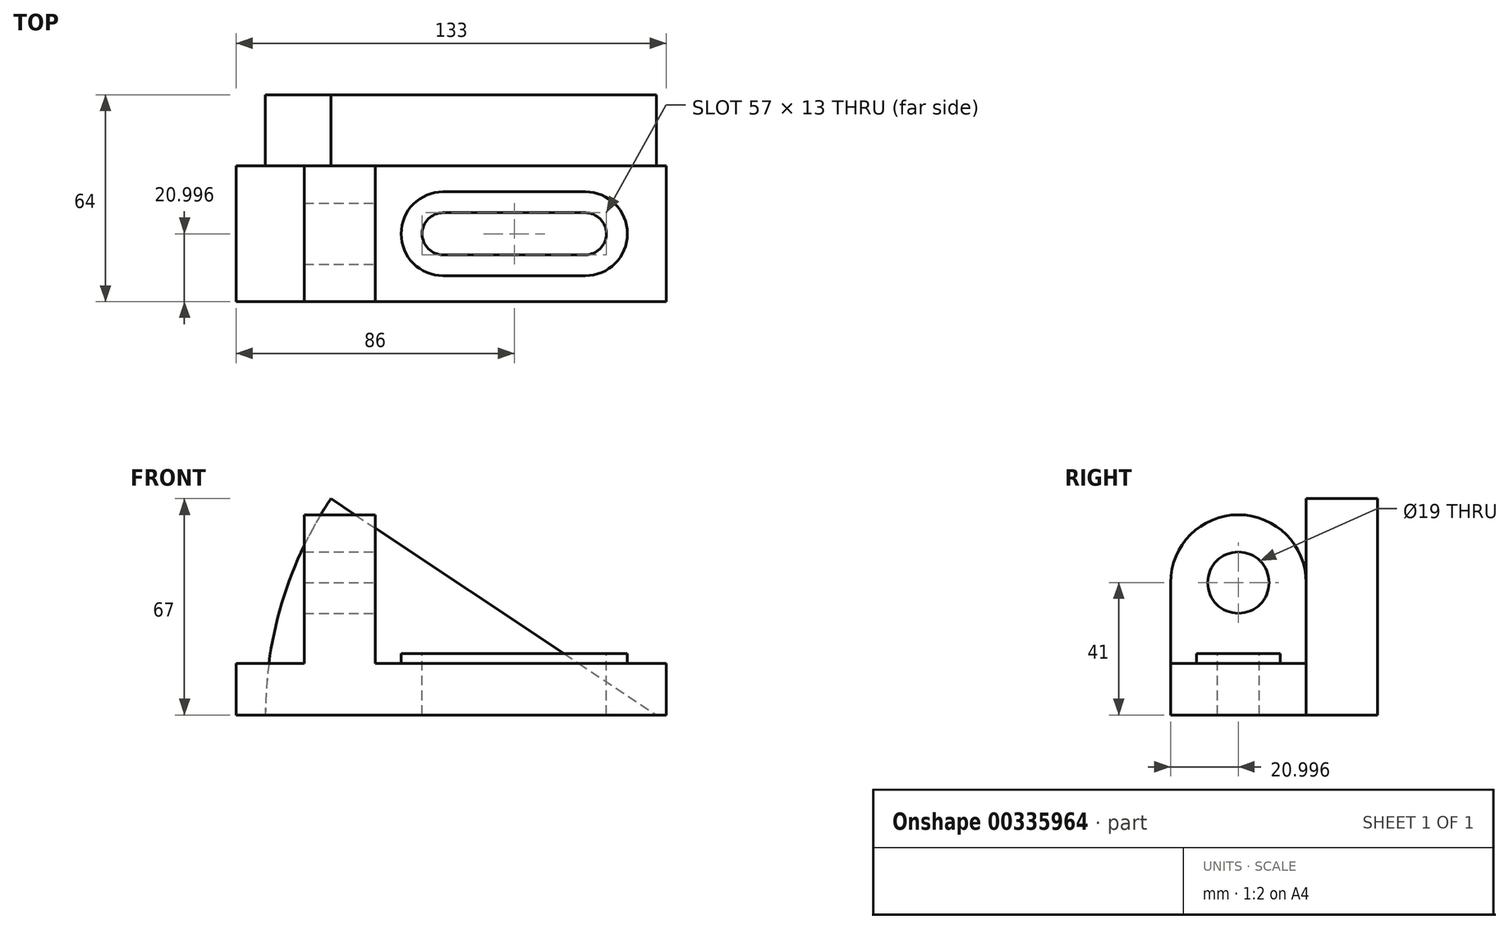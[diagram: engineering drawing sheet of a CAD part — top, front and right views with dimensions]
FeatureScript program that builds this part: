
annotation { "Feature Type Name" : "Feature", "Feature Type Description" : "" }
export const myFeature = defineFeature(function(context is Context, id is Id, definition is map)
    precondition{}
    {
        {
            var Q0;
            Q0=qCreatedBy(makeId("Right.planeOp"),FACE);
            var sketch = newSketch(context, id + "F0", { "sketchPlane" : qUnion([Q0])});
            skLineSegment(sketch, "E0.bottom", {"start": v(3.05, 24.2) * mm, "end": v(45.05, 24.2) * mm});
            skLineSegment(sketch, "E0.top", {"start": v(3.05, 8.2) * mm, "end": v(45.05, 8.2) * mm});
            skLineSegment(sketch, "E0.left", {"start": v(3.05, 24.2) * mm, "end": v(3.05, 8.2) * mm});
            skLineSegment(sketch, "E0.right", {"start": v(45.05, 24.2) * mm, "end": v(45.05, 8.2) * mm});
            skSolve(sketch);
        }
        {
            var Q0;
            Q0 = qSketchRegion(id + "F0", true);
            extrude(context, id + "F1", {"entities" : qUnion([Q0]), "oppositeDirection" : true, "depth" : 90 * mm});
        }
        {
            var Q0;
            Q0=makeQuery(id+"F1.opExtrude","CAP_FACE",FACE,{"disambiguationData":[OSD([sQuery(id+"F0.wireOp",EDGE,"E0.bottom"),sQuery(id+"F0.wireOp",EDGE,"E0.top"),sQuery(id+"F0.wireOp",EDGE,"E0.left"),sQuery(id+"F0.wireOp",EDGE,"E0.right")])],"isStart":false});
            var sketch = newSketch(context, id + "F2", { "sketchPlane" : qUnion([Q0])});
            skLineSegment(sketch, "E1", {"start": v(-45.05, 24.2) * mm, "end": v(-45.05, 49.2) * mm});
            skLineSegment(sketch, "E2", {"start": v(-45.05, 49.2) * mm, "end": v(-3.05, 49.2) * mm});
            skLineSegment(sketch, "E3", {"start": v(-3.05, 49.2) * mm, "end": v(-3.05, 24.2) * mm});
            skLineSegment(sketch, "E4", {"start": v(-3.05, 24.2) * mm, "end": v(-3.05, 8.2) * mm});
            skLineSegment(sketch, "E5", {"start": v(-3.05, 8.2) * mm, "end": v(-45.05, 8.2) * mm});
            skLineSegment(sketch, "E6", {"start": v(-45.05, 8.2) * mm, "end": v(-45.05, 24.2) * mm});
            skArc(sketch, "E7", {"start": v(-3.05, 49.2) * mm, "mid": v(-24.05, 70.2) * mm, "end": v(-45.05, 49.2) * mm});
            skCircle(sketch, "E8", {"center": v(-24.05, 49.2) * mm, "radius": 9.5 * mm});
            skSolve(sketch);
        }
        {
            var Q0;
            Q0 = qSketchRegion(id + "F2", true);
            extrude(context, id + "F3", {"entities" : qUnion([Q0]), "operationType" : NewBodyOperationType.ADD, "depth" : 22 * mm});
        }
        {
            var Q0;
            Q0=makeQuery(id+"F3.opExtrude","CAP_FACE",FACE,{"disambiguationData":[OSD([sQuery(id+"F2.wireOp",EDGE,"E1"),sQuery(id+"F2.wireOp",EDGE,"E3"),sQuery(id+"F2.wireOp",EDGE,"E4"),sQuery(id+"F2.wireOp",EDGE,"E5"),sQuery(id+"F2.wireOp",EDGE,"E6"),sQuery(id+"F2.wireOp",EDGE,"E7"),sQuery(id+"F2.wireOp",EDGE,"E8")])],"isStart":false});
            var sketch = newSketch(context, id + "F4", { "sketchPlane" : qUnion([Q0])});
            skLineSegment(sketch, "E9", {"start": v(-45.05, 8.2) * mm, "end": v(-45.05, 24.2) * mm});
            skLineSegment(sketch, "E10", {"start": v(-45.05, 24.2) * mm, "end": v(-3.05, 24.2) * mm});
            skLineSegment(sketch, "E11", {"start": v(-3.05, 24.2) * mm, "end": v(-3.05, 8.2) * mm});
            skLineSegment(sketch, "E12", {"start": v(-3.05, 8.2) * mm, "end": v(-45.05, 8.2) * mm});
            skSolve(sketch);
        }
        {
            var Q0;
            Q0 = qSketchRegion(id + "F4", true);
            extrude(context, id + "F5", {"entities" : qUnion([Q0]), "operationType" : NewBodyOperationType.ADD, "depth" : 21 * mm});
        }
        {
            var Q0;
            Q0=makeQuery(id+"F1.opExtrude","SWEPT_FACE",FACE,{"disambiguationData":[OSD([sQuery(id+"F0.wireOp",EDGE,"E0.bottom")])]});
            var sketch = newSketch(context, id + "F6", { "sketchPlane" : qUnion([Q0])});
            skArc(sketch, "E13", {"start": v(-25, 11.05) * mm, "mid": v(-12, 24.05) * mm, "end": v(-25, 37.05) * mm});
            skArc(sketch, "E14", {"start": v(-69, 37.05) * mm, "mid": v(-82, 24.05) * mm, "end": v(-69, 11.05) * mm});
            skLineSegment(sketch, "E15", {"start": v(-69, 37.05) * mm, "end": v(-25, 37.05) * mm});
            skLineSegment(sketch, "E16", {"start": v(-69, 11.05) * mm, "end": v(-25, 11.05) * mm});
            skSolve(sketch);
        }
        {
            var Q0;
            Q0 = qSketchRegion(id + "F6", true);
            extrude(context, id + "F7", {"entities" : qUnion([Q0]), "operationType" : NewBodyOperationType.ADD, "depth" : 3 * mm});
        }
        {
            var Q0;
            Q0=makeQuery(id+"F7.opExtrude","CAP_FACE",FACE,{"disambiguationData":[OSD([sQuery(id+"F6.wireOp",EDGE,"E13"),sQuery(id+"F6.wireOp",EDGE,"E14"),sQuery(id+"F6.wireOp",EDGE,"E15"),sQuery(id+"F6.wireOp",EDGE,"E16")])],"isStart":false});
            var sketch = newSketch(context, id + "F8", { "sketchPlane" : qUnion([Q0])});
            skLineSegment(sketch, "E17", {"start": v(-69, 30.55) * mm, "end": v(-25, 30.55) * mm});
            skLineSegment(sketch, "E18", {"start": v(-25, 30.55) * mm, "end": v(-25, 17.55) * mm});
            skLineSegment(sketch, "E19", {"start": v(-25, 17.55) * mm, "end": v(-69, 17.55) * mm});
            skLineSegment(sketch, "E20", {"start": v(-69, 17.55) * mm, "end": v(-69, 30.55) * mm});
            skArc(sketch, "E21", {"start": v(-69, 30.55) * mm, "mid": v(-75.5, 24.05) * mm, "end": v(-69, 17.55) * mm});
            skArc(sketch, "E22", {"start": v(-25, 17.55) * mm, "mid": v(-18.5, 24.05) * mm, "end": v(-25, 30.55) * mm});
            skSolve(sketch);
        }
        {
            var Q0;
            Q0 = qSketchRegion(id + "F8", true);
            extrude(context, id + "F9", {"entities" : qUnion([Q0]), "operationType" : NewBodyOperationType.REMOVE, "oppositeDirection" : true, "depth" : 19 * mm});
        }
        {
            var Q0;
            Q0=makeQuery(id+"F5.boolean.opBoolean","MERGE",FACE,{"derivedFrom":[makeQuery(id+"F3.boolean.opBoolean","MERGE",FACE,{"derivedFrom":[makeQuery(id+"F1.opExtrude","SWEPT_FACE",FACE,{"disambiguationData":[OSD([sQuery(id+"F0.wireOp",EDGE,"E0.right")])]}),makeQuery(id+"F3.opExtrude","SWEPT_FACE",FACE,{"disambiguationData":[OSD([sQuery(id+"F2.wireOp",EDGE,"E1"),sQuery(id+"F2.wireOp",EDGE,"E6")])]})]}),makeQuery(id+"F5.opExtrude","SWEPT_FACE",FACE,{"disambiguationData":[OSD([sQuery(id+"F4.wireOp",EDGE,"E9")])]})]});
            var sketch = newSketch(context, id + "F10", { "sketchPlane" : qUnion([Q0])});
            skArc(sketch, "E23", {"start": v(103.76, 75.2) * mm, "mid": v(118.83, 43.2) * mm, "end": v(124, 8.2) * mm});
            skLineSegment(sketch, "E24", {"start": v(103.76, 75.2) * mm, "end": v(3, 8.2) * mm});
            skSolve(sketch);
        }
        {
            var Q0;
            Q0 = qSketchRegion(id + "F10", true);
            var Q1;
            {var subQ0=sQuery(id+"F2.wireOp",EDGE,"E6");var subQ1=sQuery(id+"F2.wireOp",EDGE,"E1");var subQ2=makeQuery(id+"F3.opExtrude","CAP_EDGE",EDGE,{"disambiguationData":[OSD([subQ1,subQ0])],"isStart":true});Q1=makeQuery(id+"F10.imprint","IMPRINT",FACE,{"disambiguationData":[TD([[makeQuery(id+"F10.imprint","IMPRINT",EDGE,{"derivedFrom":subQ2}),-1.0]])]});}
            var Q2;
            {var subQ0=sQuery(id+"F2.wireOp",EDGE,"E1");var subQ3=sQuery(id+"F2.wireOp",EDGE,"E6");var subQ9=makeQuery(id+"F3.opExtrude","CAP_EDGE",EDGE,{"disambiguationData":[OSD([subQ0,subQ3])],"isStart":true});Q2=makeQuery(id+"F10.imprint","IMPRINT",FACE,{"disambiguationData":[TD([[makeQuery(id+"F10.imprint","IMPRINT",EDGE,{"derivedFrom":subQ9}),1.0]])]});}
            extrude(context, id + "F11", {"entities" : qUnion([Q0, Q1, Q2]), "operationType" : NewBodyOperationType.ADD, "depth" : 22 * mm});
        }
    });
